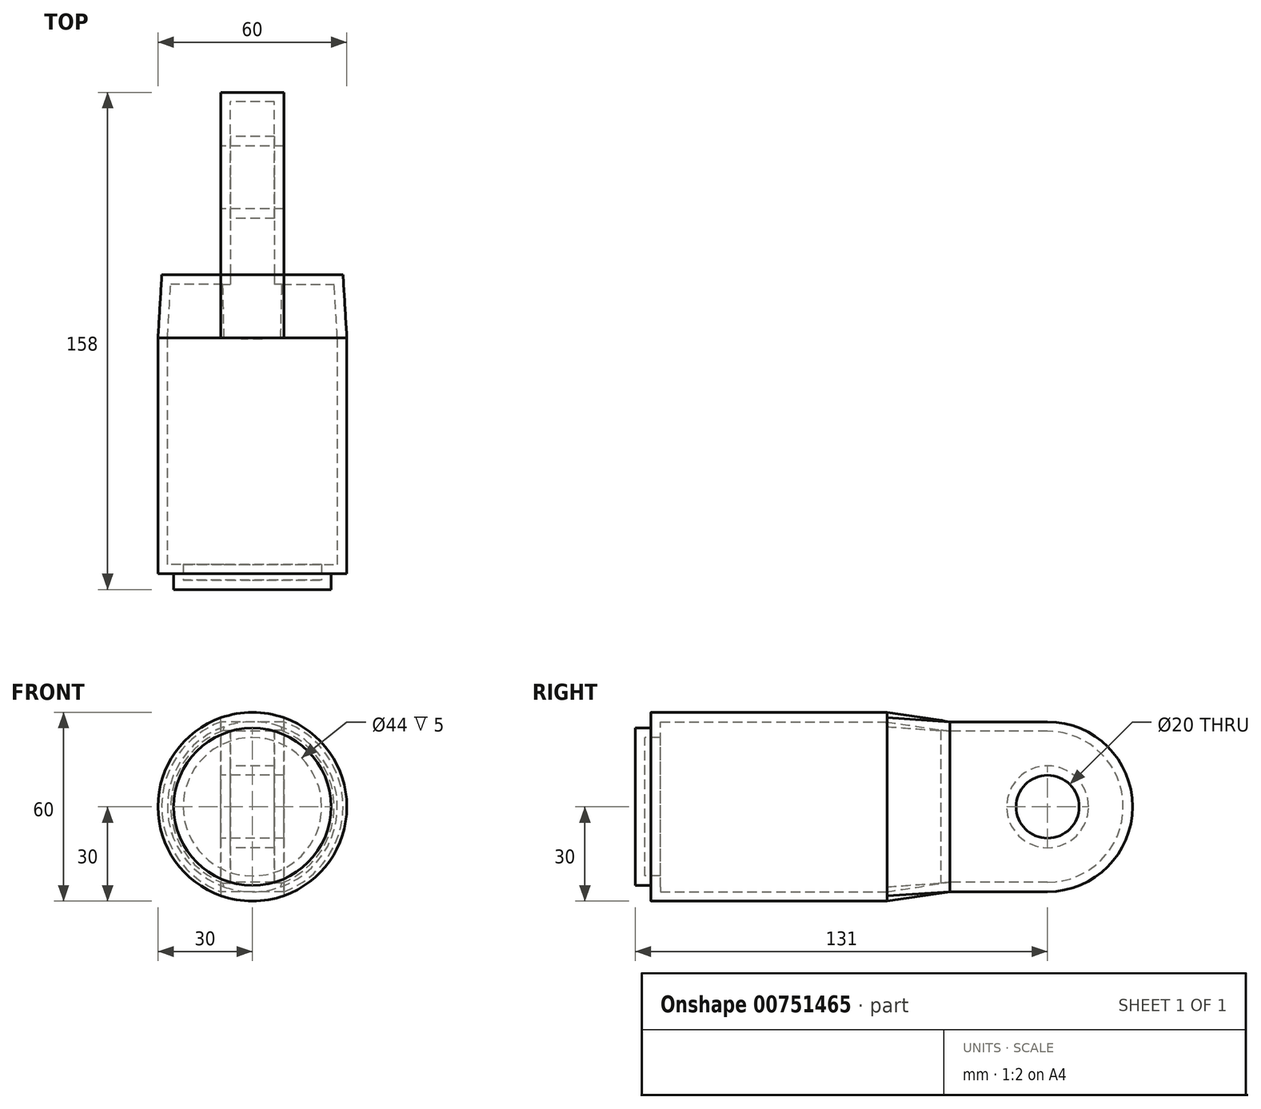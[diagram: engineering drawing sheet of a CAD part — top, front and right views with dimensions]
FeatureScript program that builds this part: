
annotation { "Feature Type Name" : "Feature", "Feature Type Description" : "" }
export const myFeature = defineFeature(function(context is Context, id is Id, definition is map)
    precondition{}
    {
        {
            var Q0;
            Q0=qCreatedBy(makeId("Right.planeOp"),FACE);
            var sketch = newSketch(context, id + "F0", { "sketchPlane" : qUnion([Q0])});
            skArc(sketch, "E0", {"start": v(0, -27) * mm, "mid": v(27, 0) * mm, "end": v(0, 27) * mm});
            skCircle(sketch, "E1", {"center": v(0, 0) * mm, "radius": 10 * mm});
            skLineSegment(sketch, "E2", {"start": v(0, 0) * mm, "end": v(-156, 0) * mm, "construction": true});
            skLineSegment(sketch, "E3", {"start": v(0, 27) * mm, "end": v(-31, 27) * mm});
            skLineSegment(sketch, "E4", {"start": v(0, -27) * mm, "end": v(-31, -27) * mm});
            skLineSegment(sketch, "E5", {"start": v(-156, -30) * mm, "end": v(-156, 30) * mm});
            skArc(sketch, "E6", {"start": v(-192.54, 33.17) * mm, "mid": v(-234, 0) * mm, "end": v(-192.54, -33.17) * mm});
            skCircle(sketch, "E7", {"center": v(0, 0) * mm, "radius": 30 * mm, "construction": true});
            skCircle(sketch, "E8", {"center": v(-200, 0) * mm, "radius": 10 * mm});
            skLineSegment(sketch, "E9", {"start": v(-31, 27) * mm, "end": v(-31, -27) * mm});
            skArc(sketch, "E10", {"start": v(-192.54, -33.17) * mm, "mid": v(-166, 0) * mm, "end": v(-192.54, 33.17) * mm, "construction": true});
            skLineSegment(sketch, "E11", {"start": v(-164, 30) * mm, "end": v(-164, -30) * mm, "construction": true});
            skLineSegment(sketch, "E12", {"start": v(-156, 30) * mm, "end": v(-164, 30) * mm});
            skLineSegment(sketch, "E13", {"start": v(-156, -30) * mm, "end": v(-164, -30) * mm});
            skArc(sketch, "E14", {"start": v(-192.54, 33.17) * mm, "mid": v(-178.36, 30.8) * mm, "end": v(-164, 30) * mm});
            skArc(sketch, "E15", {"start": v(-164, -30) * mm, "mid": v(-178.36, -30.8) * mm, "end": v(-192.54, -33.17) * mm});
            skSolve(sketch);
        }
        {
            var Q0;
            Q0=makeQuery(id+"F0.imprint","IMPRINT",FACE,{"disambiguationData":[TD([[makeQuery(id+"F0.imprint","IMPRINT",EDGE,{"derivedFrom":sQuery(id+"F0.wireOp",EDGE,"E0")}),1.0]])]});
            extrude(context, id + "F1", {"entities" : qUnion([Q0]), "endBound" : BoundingType.SYMMETRIC, "depth" : 20 * mm, "offsetDistance" : 25 * mm});
        }
        {
            var Q0;
            Q0=makeQuery(id+"F1.opExtrude","SWEPT_FACE",FACE,{"disambiguationData":[OSD([sQuery(id+"F0.wireOp",EDGE,"E9")])]});
            var sketch = newSketch(context, id + "F2", { "sketchPlane" : qUnion([Q0])});
            skCircle(sketch, "E16", {"center": v(0, 0) * mm, "radius": 30 * mm, "construction": true});
            skArc(sketch, "E17", {"start": v(-10, 27) * mm, "mid": v(-28.8, 0) * mm, "end": v(-10, -27) * mm});
            skLineSegment(sketch, "E18", {"start": v(-10, 27) * mm, "end": v(10, 27) * mm});
            skLineSegment(sketch, "E19", {"start": v(-10, -27) * mm, "end": v(10, -27) * mm});
            skLineSegment(sketch, "E20", {"start": v(0, 27) * mm, "end": v(0, -27) * mm, "construction": true});
            skArc(sketch, "E21.MirrorCS", {"start": v(10, 27) * mm, "mid": v(28.8, 0) * mm, "end": v(10, -27) * mm});
            skSolve(sketch);
        }
        {
            var Q0;
            Q0=makeQuery(id+"F2.imprint","IMPRINT",FACE,{"disambiguationData":[TD([[makeQuery(id+"F2.imprint","IMPRINT",EDGE,{"derivedFrom":sQuery(id+"F2.wireOp",EDGE,"E18")}),1.0]])]});
            cPlane(context, id + "F3", {"entities" : qUnion([Q0]), "cplaneType" : CPlaneType.OFFSET, "offset" : 20 * mm, "width" : 150 * mm, "height" : 150 * mm});
        }
        {
            var Q0;
            Q0=qCreatedBy(id+"F3.planeOp",FACE);
            var sketch = newSketch(context, id + "F4", { "sketchPlane" : qUnion([Q0])});
            skArc(sketch, "E22.0", {"start": v(-10, 28.28) * mm, "mid": v(-30, 0) * mm, "end": v(-10, -28.28) * mm});
            skLineSegment(sketch, "E23", {"start": v(-10, 28.28) * mm, "end": v(-10, -28.28) * mm});
            skLineSegment(sketch, "E24", {"start": v(10, 28.28) * mm, "end": v(10, -28.28) * mm});
            skArc(sketch, "E25.trimOffspring", {"start": v(10, -28.28) * mm, "mid": v(30, 0) * mm, "end": v(10, 28.28) * mm});
            skArc(sketch, "E26", {"start": v(10, 28.28) * mm, "mid": v(0, 30) * mm, "end": v(-10, 28.28) * mm});
            skArc(sketch, "E27", {"start": v(-10, -28.28) * mm, "mid": v(0, -30) * mm, "end": v(10, -28.28) * mm});
            skSolve(sketch);
        }
        {
            var Q1;
            Q1 = qSketchRegion(id + "F2", true);
            var Q2;
            Q2 = qSketchRegion(id + "F4", true);
            loft(context, id + "F5", {"operationType" : NewBodyOperationType.ADD, "sheetProfilesArray" : [{ "sheetProfileEntities" : qUnion([Q1]) }, { "sheetProfileEntities" : qUnion([Q2]) }]});
        }
        {
            var Q0;
            {var subQ0=makeQuery(id+"F4.imprint","IMPRINT",EDGE,{"derivedFrom":sQuery(id+"F4.wireOp",EDGE,"E23")});var subQ1=makeQuery(id+"F4.imprint","IMPRINT",EDGE,{"derivedFrom":sQuery(id+"F4.wireOp",EDGE,"E24")});Q0=makeQuery(id+"F5.opLoft","CAP_FACE",FACE,{"disambiguationData":[OSD([makeQuery(id+"F4.imprint","IMPRINT",FACE,{"disambiguationData":[TD([[makeQuery(id+"F4.imprint","IMPRINT",EDGE,{"derivedFrom":sQuery(id+"F4.wireOp",EDGE,"E22.0")}),1.0]])]}),makeQuery(id+"F4.imprint","IMPRINT",FACE,{"disambiguationData":[TD([[subQ1,1.0]])]}),makeQuery(id+"F4.imprint","IMPRINT",FACE,{"disambiguationData":[TD([[subQ0,1.0]])]})])],"isStart":true});}
            var Q1;
            Q1=makeQuery(id+"Flma1KrjLcidEWh_1.opExtrude","SWEPT_FACE",FACE,{"disambiguationData":[OSD([sQuery(id+"F0.wireOp",EDGE,"E5")])]});
            extrude(context, id + "F6", {"entities" : qUnion([Q0]), "operationType" : NewBodyOperationType.ADD, "depth" : 80 * mm, "endBoundEntityFace" : qUnion([Q1]), "offsetDistance" : 25 * mm});
        }
        {
            var Q0;
            {var subQ0=makeQuery(id+"F4.imprint","IMPRINT",EDGE,{"derivedFrom":sQuery(id+"F4.wireOp",EDGE,"E23")});var subQ1=makeQuery(id+"F4.imprint","IMPRINT",EDGE,{"derivedFrom":sQuery(id+"F4.wireOp",EDGE,"E24")});Q0=makeQuery(id+"F6.opExtrude","CAP_FACE",FACE,{"disambiguationData":[OSD([makeQuery(id+"F4.imprint","IMPRINT",FACE,{"disambiguationData":[TD([[makeQuery(id+"F4.imprint","IMPRINT",EDGE,{"derivedFrom":sQuery(id+"F4.wireOp",EDGE,"E22.0")}),1.0]])]}),makeQuery(id+"F4.imprint","IMPRINT",FACE,{"disambiguationData":[TD([[subQ1,1.0]])]}),makeQuery(id+"F4.imprint","IMPRINT",FACE,{"disambiguationData":[TD([[subQ0,1.0]])]})])],"isStart":false});}
            var sketch = newSketch(context, id + "F7", { "sketchPlane" : qUnion([Q0])});
            skCircle(sketch, "E28", {"center": v(0, 0) * mm, "radius": 25 * mm});
            skCircle(sketch, "E29", {"center": v(0, 0) * mm, "radius": 35 * mm});
            skSolve(sketch);
        }
        {
            var Q0;
            Q0 = qSketchRegion(id + "F7", true);
            extrude(context, id + "F8", {"entities" : qUnion([Q0]), "operationType" : NewBodyOperationType.REMOVE, "oppositeDirection" : true, "depth" : 5 * mm, "offsetDistance" : 25 * mm});
        }
        {
            var Q0;
            Q0=makeQuery(id+"F6.opExtrude","SWEPT_FACE",FACE,{"disambiguationData":[OSD([sQuery(id+"F4.wireOp",EDGE,"E24"),sQuery(id+"F4.wireOp",EDGE,"E25.trimOffspring"),sQuery(id+"F4.wireOp",EDGE,"E26"),sQuery(id+"F4.wireOp",EDGE,"E27")])]});
            var Q1;
            Q1=makeQuery(id+"F1.opExtrude","SWEPT_BODY",BODY,{"disambiguationData":[OSD([sQuery(id+"F0.wireOp",EDGE,"E0"),sQuery(id+"F0.wireOp",EDGE,"E1"),sQuery(id+"F0.wireOp",EDGE,"E3"),sQuery(id+"F0.wireOp",EDGE,"E4"),sQuery(id+"F0.wireOp",EDGE,"E9")])]});
            shell(context, id + "F9", {"isHollow" : true, "entities" : qUnion([Q0]), "parts" : qUnion([Q1]), "thickness" : 3 * mm});
        }
    });
